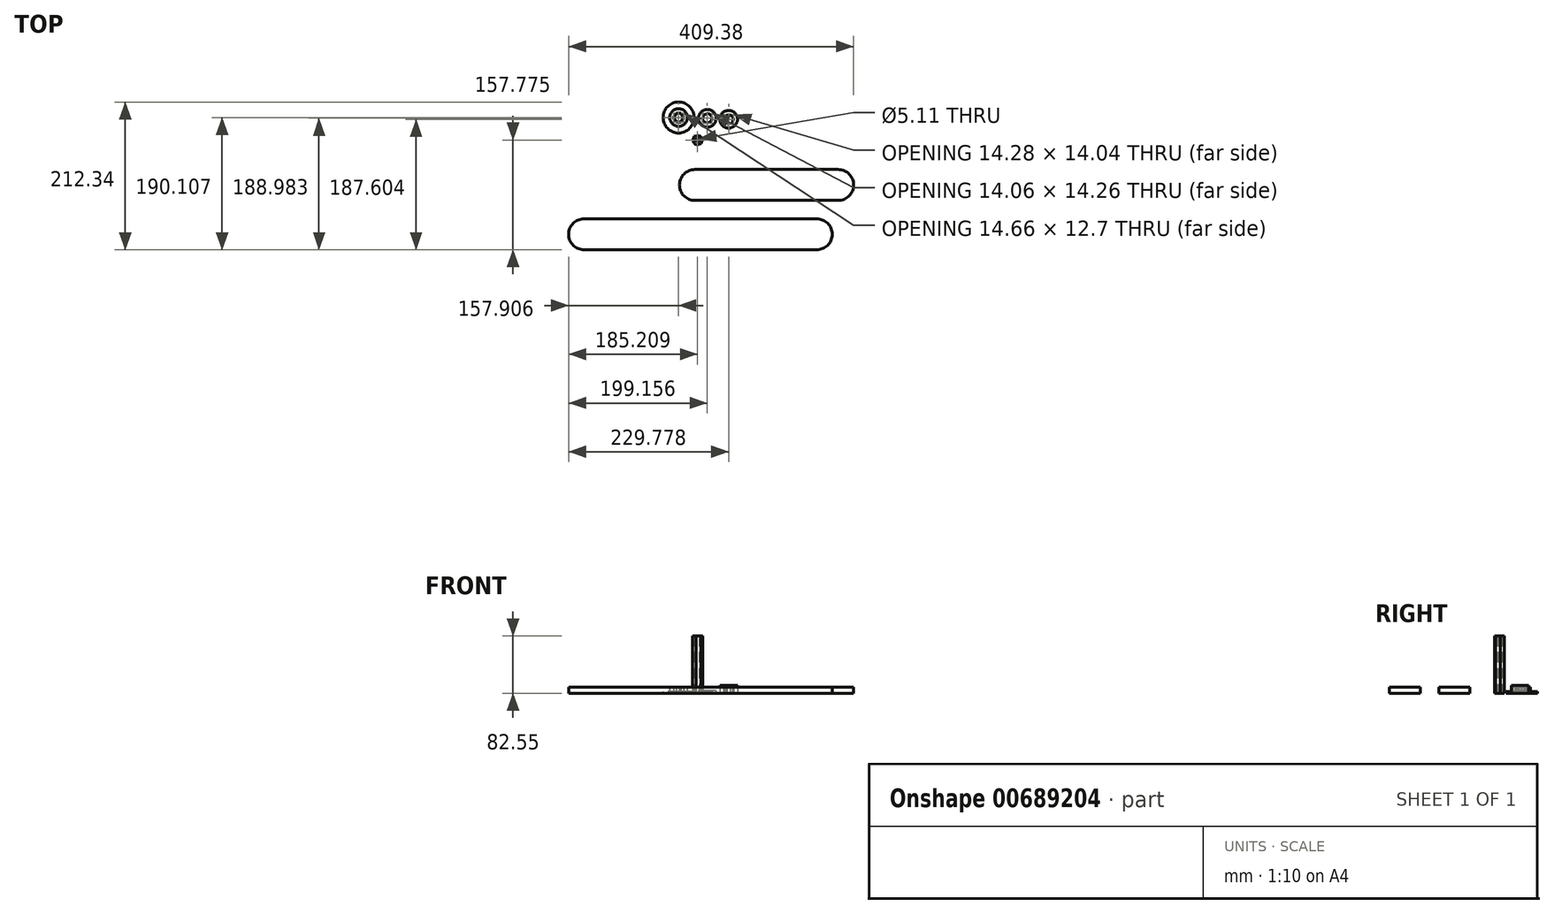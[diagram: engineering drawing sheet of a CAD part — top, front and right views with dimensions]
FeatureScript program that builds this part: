
annotation { "Feature Type Name" : "Feature", "Feature Type Description" : "" }
export const myFeature = defineFeature(function(context is Context, id is Id, definition is map)
    precondition{}
    {
        {
            var Q0;
            Q0=qCreatedBy(makeId("Top.planeOp"),FACE);
            var sketch = newSketch(context, id + "F0", { "sketchPlane" : qUnion([Q0])});
            skCircle(sketch, "E0", {"center": v(-57.7, 58.67) * mm, "radius": 22.24 * mm});
            skCircle(sketch, "E1.cCircle", {"center": v(-57.7, 58.67) * mm, "radius": 6.35 * mm, "construction": true});
            skLineSegment(sketch, "E1.0", {"start": v(-54.03, 52.32) * mm, "end": v(-61.36, 52.32) * mm});
            skLineSegment(sketch, "E1.1", {"start": v(-61.36, 52.32) * mm, "end": v(-65.03, 58.67) * mm});
            skLineSegment(sketch, "E1.2", {"start": v(-65.03, 58.67) * mm, "end": v(-61.36, 65.02) * mm});
            skLineSegment(sketch, "E1.3", {"start": v(-61.36, 65.02) * mm, "end": v(-54.03, 65.02) * mm});
            skLineSegment(sketch, "E1.4", {"start": v(-54.03, 65.02) * mm, "end": v(-50.36, 58.67) * mm});
            skLineSegment(sketch, "E1.5", {"start": v(-50.36, 58.67) * mm, "end": v(-54.03, 52.32) * mm});
            skPoint(sketch, "E1.0.midPoint", {"position": v(-57.7, 52.32) * mm});
            skSolve(sketch);
        }
        {
            var Q0;
            Q0=makeQuery(id+"F0.imprint","IMPRINT",FACE,{"disambiguationData":[TD([[makeQuery(id+"F0.imprint","IMPRINT",EDGE,{"derivedFrom":sQuery(id+"F0.wireOp",EDGE,"E0")}),1.0]])]});
            extrude(context, id + "F1", {"entities" : qUnion([Q0]), "depth" : 2.8 * mm, "offsetDistance" : 25.4 * mm});
        }
        {
            var Q0;
            Q0=makeQuery(id+"F1.opExtrude","CAP_FACE",FACE,{"disambiguationData":[OSD([sQuery(id+"F0.wireOp",EDGE,"E0"),sQuery(id+"F0.wireOp",EDGE,"E1.0"),sQuery(id+"F0.wireOp",EDGE,"E1.1"),sQuery(id+"F0.wireOp",EDGE,"E1.2"),sQuery(id+"F0.wireOp",EDGE,"E1.3"),sQuery(id+"F0.wireOp",EDGE,"E1.4"),sQuery(id+"F0.wireOp",EDGE,"E1.5")])],"isStart":false});
            var sketch = newSketch(context, id + "F2", { "sketchPlane" : qUnion([Q0])});
            skCircle(sketch, "E2.0.0", {"center": v(-57.7, 58.67) * mm, "radius": 22.24 * mm});
            skLineSegment(sketch, "E3.0", {"start": v(-61.36, 65.02) * mm, "end": v(-54.03, 65.02) * mm});
            skLineSegment(sketch, "E4.0", {"start": v(-54.03, 65.02) * mm, "end": v(-50.36, 58.67) * mm});
            skLineSegment(sketch, "E5.0", {"start": v(-50.36, 58.67) * mm, "end": v(-54.03, 52.32) * mm});
            skLineSegment(sketch, "E6.0", {"start": v(-54.03, 52.32) * mm, "end": v(-61.36, 52.32) * mm});
            skLineSegment(sketch, "E7.0", {"start": v(-61.36, 52.32) * mm, "end": v(-65.03, 58.67) * mm});
            skLineSegment(sketch, "E8.0", {"start": v(-65.03, 58.67) * mm, "end": v(-61.36, 65.02) * mm});
            skCircle(sketch, "E9", {"center": v(-57.7, 58.67) * mm, "radius": 12.7 * mm});
            skSolve(sketch);
        }
        {
            var Q0;
            Q0=makeQuery(id+"F2.imprint","IMPRINT",FACE,{"disambiguationData":[TD([[makeQuery(id+"F2.imprint","IMPRINT",EDGE,{"derivedFrom":sQuery(id+"F2.wireOp",EDGE,"E3.0")}),1.0]])]});
            extrude(context, id + "F3", {"entities" : qUnion([Q0]), "operationType" : NewBodyOperationType.ADD, "depth" : 6.35 * mm, "offsetDistance" : 25.4 * mm});
        }
        {
            var Q0;
            Q0=qCreatedBy(makeId("Top.planeOp"),FACE);
            var sketch = newSketch(context, id + "F4", { "sketchPlane" : qUnion([Q0])});
            skCircle(sketch, "E10", {"center": v(-16.44, 57.54) * mm, "radius": 12.7 * mm});
            skCircle(sketch, "E11.cCircle", {"center": v(-16.44, 57.54) * mm, "radius": 6.35 * mm, "construction": true});
            skLineSegment(sketch, "E11.0", {"start": v(-11.13, 52.5) * mm, "end": v(-18.16, 50.41) * mm});
            skLineSegment(sketch, "E11.1", {"start": v(-18.16, 50.41) * mm, "end": v(-23.48, 55.47) * mm});
            skLineSegment(sketch, "E11.2", {"start": v(-23.48, 55.47) * mm, "end": v(-21.76, 62.6) * mm});
            skLineSegment(sketch, "E11.3", {"start": v(-21.76, 62.6) * mm, "end": v(-14.73, 64.67) * mm});
            skLineSegment(sketch, "E11.4", {"start": v(-14.73, 64.67) * mm, "end": v(-9.41, 59.62) * mm});
            skLineSegment(sketch, "E11.5", {"start": v(-9.41, 59.62) * mm, "end": v(-11.13, 52.5) * mm});
            skPoint(sketch, "E11.0.midPoint", {"position": v(-14.64, 51.45) * mm});
            skSolve(sketch);
        }
        {
            var Q0;
            Q0=qSketchRegion(id+"F4",true);
            extrude(context, id + "F5", {"entities" : qUnion([Q0]), "depth" : 3.8 * mm, "offsetDistance" : 25.4 * mm});
        }
        {
            var Q0;
            Q0=qCreatedBy(makeId("Top.planeOp"),FACE);
            var sketch = newSketch(context, id + "F6", { "sketchPlane" : qUnion([Q0])});
            skCircle(sketch, "E12.cCircle", {"center": v(-30.4, 26.34) * mm, "radius": 6.35 * mm, "construction": true});
            skLineSegment(sketch, "E12.0", {"start": v(-25.43, 20.93) * mm, "end": v(-32.6, 19.34) * mm});
            skLineSegment(sketch, "E12.1", {"start": v(-32.6, 19.34) * mm, "end": v(-37.55, 24.74) * mm});
            skLineSegment(sketch, "E12.2", {"start": v(-37.55, 24.74) * mm, "end": v(-35.35, 31.74) * mm});
            skLineSegment(sketch, "E12.3", {"start": v(-35.35, 31.74) * mm, "end": v(-28.19, 33.33) * mm});
            skLineSegment(sketch, "E12.4", {"start": v(-28.19, 33.33) * mm, "end": v(-23.23, 27.93) * mm});
            skLineSegment(sketch, "E12.5", {"start": v(-23.23, 27.93) * mm, "end": v(-25.43, 20.93) * mm});
            skPoint(sketch, "E12.0.midPoint", {"position": v(-29.01, 20.14) * mm});
            skCircle(sketch, "E13", {"center": v(-30.4, 26.34) * mm, "radius": 2.55 * mm});
            skSolve(sketch);
        }
        {
            var Q0;
            Q0=qSketchRegion(id+"F6",true);
            extrude(context, id + "F7", {"entities" : qUnion([Q0]), "depth" : 82.55 * mm, "offsetDistance" : 25.4 * mm});
        }
        {
            var Q0;
            Q0=qCreatedBy(makeId("Top.planeOp"),FACE);
            var sketch = newSketch(context, id + "F8", { "sketchPlane" : qUnion([Q0])});
            skCircle(sketch, "E14", {"center": v(14.18, 56.16) * mm, "radius": 12.7 * mm});
            skCircle(sketch, "E15.cCircle", {"center": v(14.18, 56.16) * mm, "radius": 6.35 * mm, "construction": true});
            skLineSegment(sketch, "E15.0", {"start": v(19.2, 50.82) * mm, "end": v(12.05, 49.15) * mm});
            skLineSegment(sketch, "E15.1", {"start": v(12.05, 49.15) * mm, "end": v(7.04, 54.5) * mm});
            skLineSegment(sketch, "E15.2", {"start": v(7.04, 54.5) * mm, "end": v(9.16, 61.51) * mm});
            skLineSegment(sketch, "E15.3", {"start": v(9.16, 61.51) * mm, "end": v(16.3, 63.18) * mm});
            skLineSegment(sketch, "E15.4", {"start": v(16.3, 63.18) * mm, "end": v(21.32, 57.83) * mm});
            skLineSegment(sketch, "E15.5", {"start": v(21.32, 57.83) * mm, "end": v(19.2, 50.82) * mm});
            skPoint(sketch, "E15.0.midPoint", {"position": v(15.62, 49.98) * mm});
            skSolve(sketch);
        }
        {
            var Q0;
            Q0=makeQuery(id+"F8.imprint","IMPRINT",FACE,{"disambiguationData":[TD([[makeQuery(id+"F8.imprint","IMPRINT",EDGE,{"derivedFrom":sQuery(id+"F8.wireOp",EDGE,"E14")}),1.0]])]});
            extrude(context, id + "F9", {"entities" : qUnion([Q0]), "depth" : 11.6 * mm, "offsetDistance" : 25.4 * mm});
        }
        {
            var Q0;
            Q0=qCreatedBy(makeId("Top.planeOp"),FACE);
            var sketch = newSketch(context, id + "F10", { "sketchPlane" : qUnion([Q0])});
            skLineSegment(sketch, "E16", {"start": v(-34.2, -38.3) * mm, "end": v(171.54, -38.3) * mm});
            skLineSegment(sketch, "E17", {"start": v(-193.36, -109.2) * mm, "end": v(140.66, -109.2) * mm});
            skArc(sketch, "E18.0.startCap", {"start": v(-193.36, -131.44) * mm, "mid": v(-215.6, -109.2) * mm, "end": v(-193.36, -86.96) * mm});
            skArc(sketch, "E18.0.endCap", {"start": v(140.66, -86.96) * mm, "mid": v(162.9, -109.2) * mm, "end": v(140.66, -131.44) * mm});
            skLineSegment(sketch, "E18.0.left", {"start": v(-193.36, -86.96) * mm, "end": v(140.66, -86.96) * mm});
            skLineSegment(sketch, "E18.0.right", {"start": v(-193.36, -131.44) * mm, "end": v(140.66, -131.44) * mm});
            skArc(sketch, "E18.1.startCap", {"start": v(-34.2, -60.53) * mm, "mid": v(-56.43, -38.3) * mm, "end": v(-34.2, -16.06) * mm});
            skArc(sketch, "E18.1.endCap", {"start": v(171.54, -16.06) * mm, "mid": v(193.78, -38.3) * mm, "end": v(171.54, -60.53) * mm});
            skLineSegment(sketch, "E18.1.left", {"start": v(-34.2, -16.06) * mm, "end": v(171.54, -16.06) * mm});
            skLineSegment(sketch, "E18.1.right", {"start": v(-34.2, -60.53) * mm, "end": v(171.54, -60.53) * mm});
            skArc(sketch, "E19.0", {"start": v(-193.36, -136.06) * mm, "mid": v(-220.23, -109.2) * mm, "end": v(-193.36, -82.34) * mm});
            skLineSegment(sketch, "E19.1", {"start": v(-193.36, -136.06) * mm, "end": v(140.66, -136.06) * mm});
            skArc(sketch, "E19.2", {"start": v(140.66, -82.34) * mm, "mid": v(167.52, -109.2) * mm, "end": v(140.66, -136.06) * mm});
            skLineSegment(sketch, "E19.3", {"start": v(-193.36, -82.34) * mm, "end": v(140.66, -82.34) * mm});
            skLineSegment(sketch, "E20.0", {"start": v(-34.2, -11.43) * mm, "end": v(171.54, -11.43) * mm});
            skArc(sketch, "E20.1", {"start": v(-34.2, -65.16) * mm, "mid": v(-61.06, -38.3) * mm, "end": v(-34.2, -11.43) * mm});
            skLineSegment(sketch, "E20.2", {"start": v(-34.2, -65.16) * mm, "end": v(171.54, -65.16) * mm});
            skArc(sketch, "E20.3", {"start": v(171.54, -11.43) * mm, "mid": v(198.4, -38.3) * mm, "end": v(171.54, -65.16) * mm});
            skSolve(sketch);
        }
        {
            var Q0;
            Q0=makeQuery(id+"F10.imprint","IMPRINT",FACE,{"disambiguationData":[TD([[makeQuery(id+"F10.imprint","IMPRINT",EDGE,{"derivedFrom":sQuery(id+"F10.wireOp",EDGE,"E18.1.startCap")}),1.0]])]});
            extrude(context, id + "F11", {"entities" : qUnion([Q0]), "depth" : 8.9 * mm, "offsetDistance" : 25.4 * mm});
        }
        {
            var Q0;
            Q0=makeQuery(id+"F10.imprint","IMPRINT",FACE,{"disambiguationData":[TD([[makeQuery(id+"F10.imprint","IMPRINT",EDGE,{"derivedFrom":sQuery(id+"F10.wireOp",EDGE,"E18.0.startCap")}),1.0]])]});
            extrude(context, id + "F12", {"entities" : qUnion([Q0]), "depth" : 8.9 * mm, "offsetDistance" : 25.4 * mm});
        }
    });
